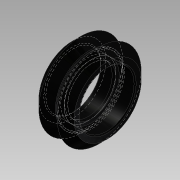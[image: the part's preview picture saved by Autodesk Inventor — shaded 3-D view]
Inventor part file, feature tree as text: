
AUTODESK INVENTOR PART (.ipt)
format: ipt  version: 2013 SP2 (Build 170200200, 200)  size: 137,216 bytes
history: native  units: mm
features: revolve x1, sketch x1
ambient origin geometry x8: Origin, YZ Plane, XZ Plane, XY Plane, X Axis, Y Axis, Z Axis, Center Point
bodies: Solid1 (feature_tree)
feature tree (2):
  revolve  "Revolution1"  [1 undecoded]
  sketch  "Sketch1"  dims[d0=10.0mm d2=0.5mm d3=15.974mm d4=13.89mm d5=0.3mm d6=0.3mm d7=19.54mm d8=5.12mm d12=24.39mm d14=18.75mm d16=0.275mm d17=135.0deg d18=135.0deg d19=2.695mm d20=90.0deg]
note: 1 required parameter value undecoded (feature->parameter linkage not recoverable at this tier; creation-order binding heuristic only, values carry confidence <= 0.55)
